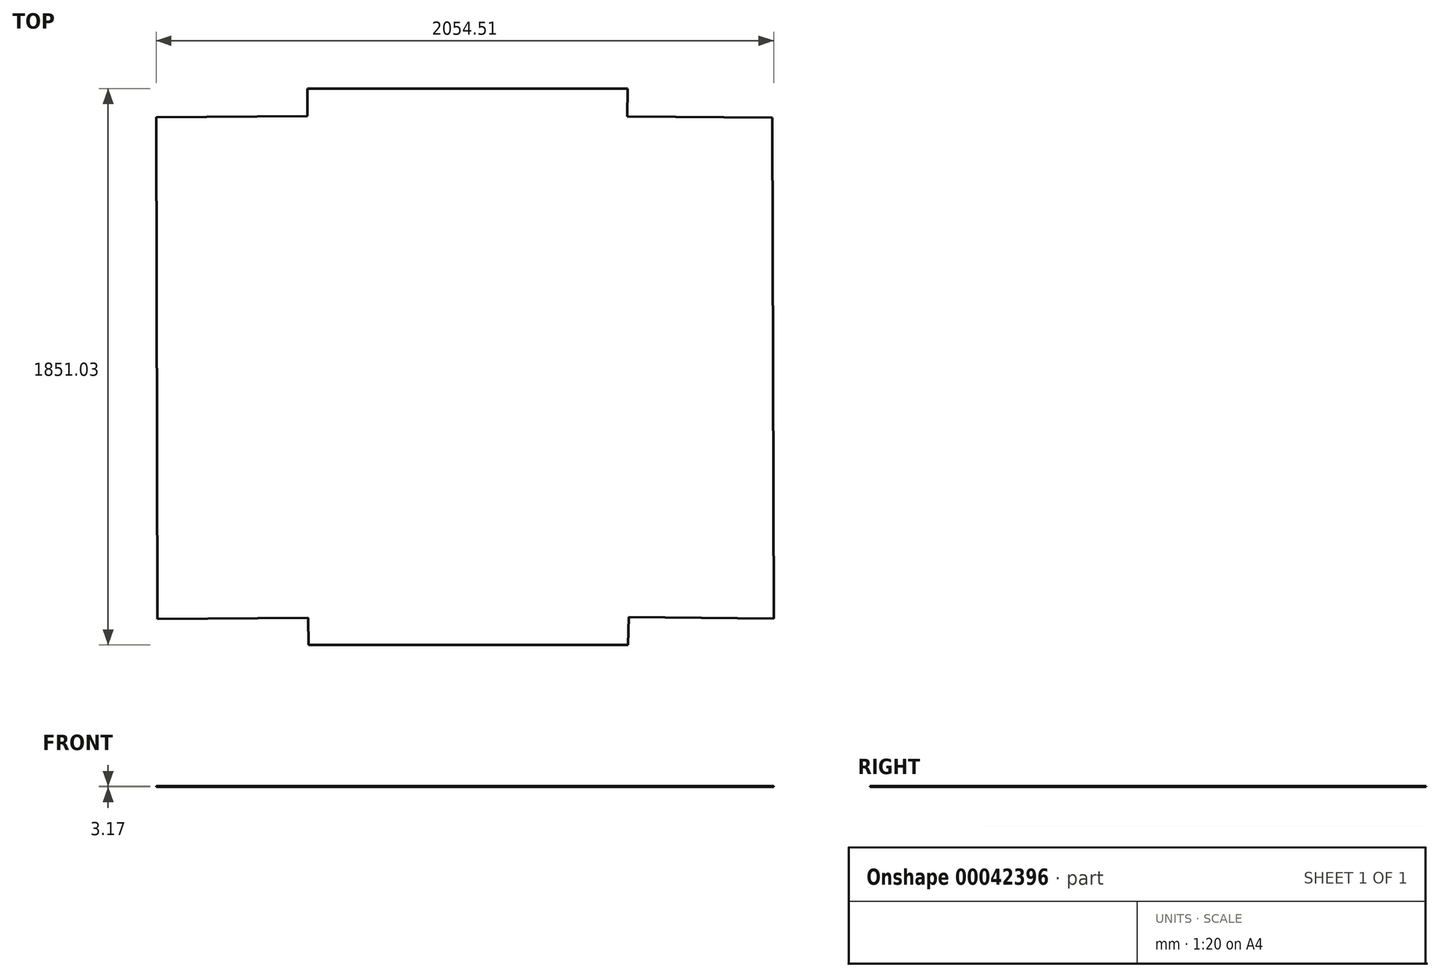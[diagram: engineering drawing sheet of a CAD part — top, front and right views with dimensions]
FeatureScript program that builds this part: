
annotation { "Feature Type Name" : "Feature", "Feature Type Description" : "" }
export const myFeature = defineFeature(function(context is Context, id is Id, definition is map)
    precondition{}
    {
        {
            var Q0;
            Q0=qCreatedBy(makeId("Top.planeOp"),FACE);
            var sketch = newSketch(context, id + "F0", { "sketchPlane" : qUnion([Q0])});
            skLineSegment(sketch, "E0", {"start": v(-537.46, 931.43) * mm, "end": v(530.93, 931.43) * mm});
            skLineSegment(sketch, "E1", {"start": v(-533.42, -922.77) * mm, "end": v(533.38, -922.77) * mm});
            skLineSegment(sketch, "E2", {"start": v(1012.74, 835.02) * mm, "end": v(1017.74, -835.02) * mm});
            skPoint(sketch, "E3", {"position": v(1015.24, 0) * mm});
            skLineSegment(sketch, "E4", {"start": v(-1039.96, 836.61) * mm, "end": v(-1036.77, -836.61) * mm});
            skPoint(sketch, "E5", {"position": v(-1038.36, 0) * mm});
            skLineSegment(sketch, "E6", {"start": v(-1039.96, 836.61) * mm, "end": v(-536.74, 840.95) * mm});
            skLineSegment(sketch, "E7", {"start": v(-536.74, 840.95) * mm, "end": v(-537.46, 931.43) * mm});
            skLineSegment(sketch, "E8", {"start": v(530.93, 931.43) * mm, "end": v(530.16, 839.36) * mm});
            skLineSegment(sketch, "E9", {"start": v(530.16, 839.36) * mm, "end": v(1012.74, 835.02) * mm});
            skLineSegment(sketch, "E10", {"start": v(1017.74, -835.02) * mm, "end": v(535.16, -830.7) * mm});
            skLineSegment(sketch, "E11", {"start": v(535.16, -830.7) * mm, "end": v(533.38, -922.77) * mm});
            skLineSegment(sketch, "E12", {"start": v(-533.42, -922.77) * mm, "end": v(-535.14, -832.3) * mm});
            skLineSegment(sketch, "E13", {"start": v(-535.14, -832.3) * mm, "end": v(-1036.77, -836.61) * mm});
            skSolve(sketch);
        }
        {
            var Q0;
            Q0=makeQuery(id+"F0.imprint","IMPRINT",FACE,{"disambiguationData":[TD([[makeQuery(id+"F0.imprint","IMPRINT",EDGE,{"derivedFrom":sQuery(id+"F0.wireOp",EDGE,"E0")}),-1.0]])]});
            var sketch = newSketch(context, id + "F1", { "sketchPlane" : qUnion([Q0])});
            skLineSegment(sketch, "E14.0", {"start": v(528.56, 837.79) * mm, "end": v(529.33, 929.85) * mm});
            skLineSegment(sketch, "E14.1", {"start": v(-1035.18, -835) * mm, "end": v(-533.58, -830.7) * mm});
            skLineSegment(sketch, "E14.2", {"start": v(-1038.36, 835.04) * mm, "end": v(-1035.18, -835) * mm});
            skLineSegment(sketch, "E14.3", {"start": v(-535.14, 839.38) * mm, "end": v(-1038.36, 835.04) * mm});
            skLineSegment(sketch, "E14.4", {"start": v(-535.86, 929.85) * mm, "end": v(-535.14, 839.38) * mm});
            skLineSegment(sketch, "E14.5", {"start": v(-533.58, -830.7) * mm, "end": v(-531.86, -921.18) * mm});
            skLineSegment(sketch, "E14.6", {"start": v(529.33, 929.85) * mm, "end": v(-535.86, 929.85) * mm});
            skLineSegment(sketch, "E14.7", {"start": v(-531.86, -921.18) * mm, "end": v(531.82, -921.18) * mm});
            skLineSegment(sketch, "E14.8", {"start": v(531.82, -921.18) * mm, "end": v(533.6, -829.1) * mm});
            skLineSegment(sketch, "E14.9", {"start": v(533.6, -829.1) * mm, "end": v(1016.15, -833.42) * mm});
            skLineSegment(sketch, "E14.10", {"start": v(1016.15, -833.42) * mm, "end": v(1011.16, 833.45) * mm});
            skLineSegment(sketch, "E14.11", {"start": v(1011.16, 833.45) * mm, "end": v(528.56, 837.79) * mm});
            skSolve(sketch);
        }
        {
            var Q0;
            Q0 = qSketchRegion(id + "F1", true);
            extrude(context, id + "F2", {"entities" : qUnion([Q0]), "depth" : 3.17 * mm});
        }
    });
